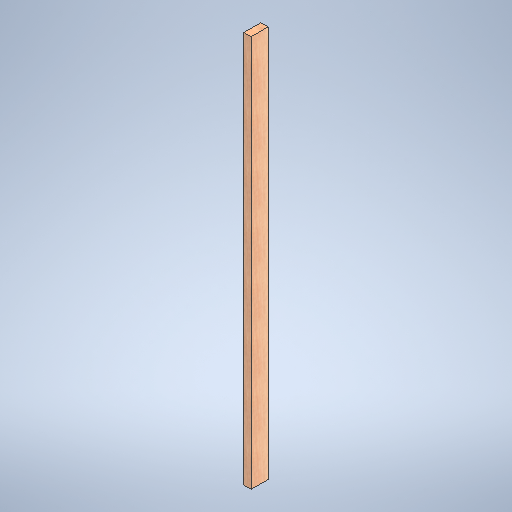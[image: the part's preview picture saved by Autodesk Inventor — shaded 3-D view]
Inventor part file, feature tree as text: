
AUTODESK INVENTOR PART (.ipt)
format: ipt  version: 2025.1 (Build 291241020, 241B)  size: 285,184 bytes
history: native  units: in
note: dims shown in document units (in); Inventor stores cm internally (conversion verified against a paired STEP export)
features: extrude x1, sketch x1
ambient origin geometry x8: Origin, YZ Plane, XZ Plane, XY Plane, X Axis, Y Axis, Z Axis, Center Point
bodies: Solid1 (feature_tree)
feature tree (2):
  extrude  "Extrusion1"  Depth=1.5in
  sketch  "Sketch1"  dims[d0=3.5in d1=1.5in d2=80.5in d3=0.0in]
